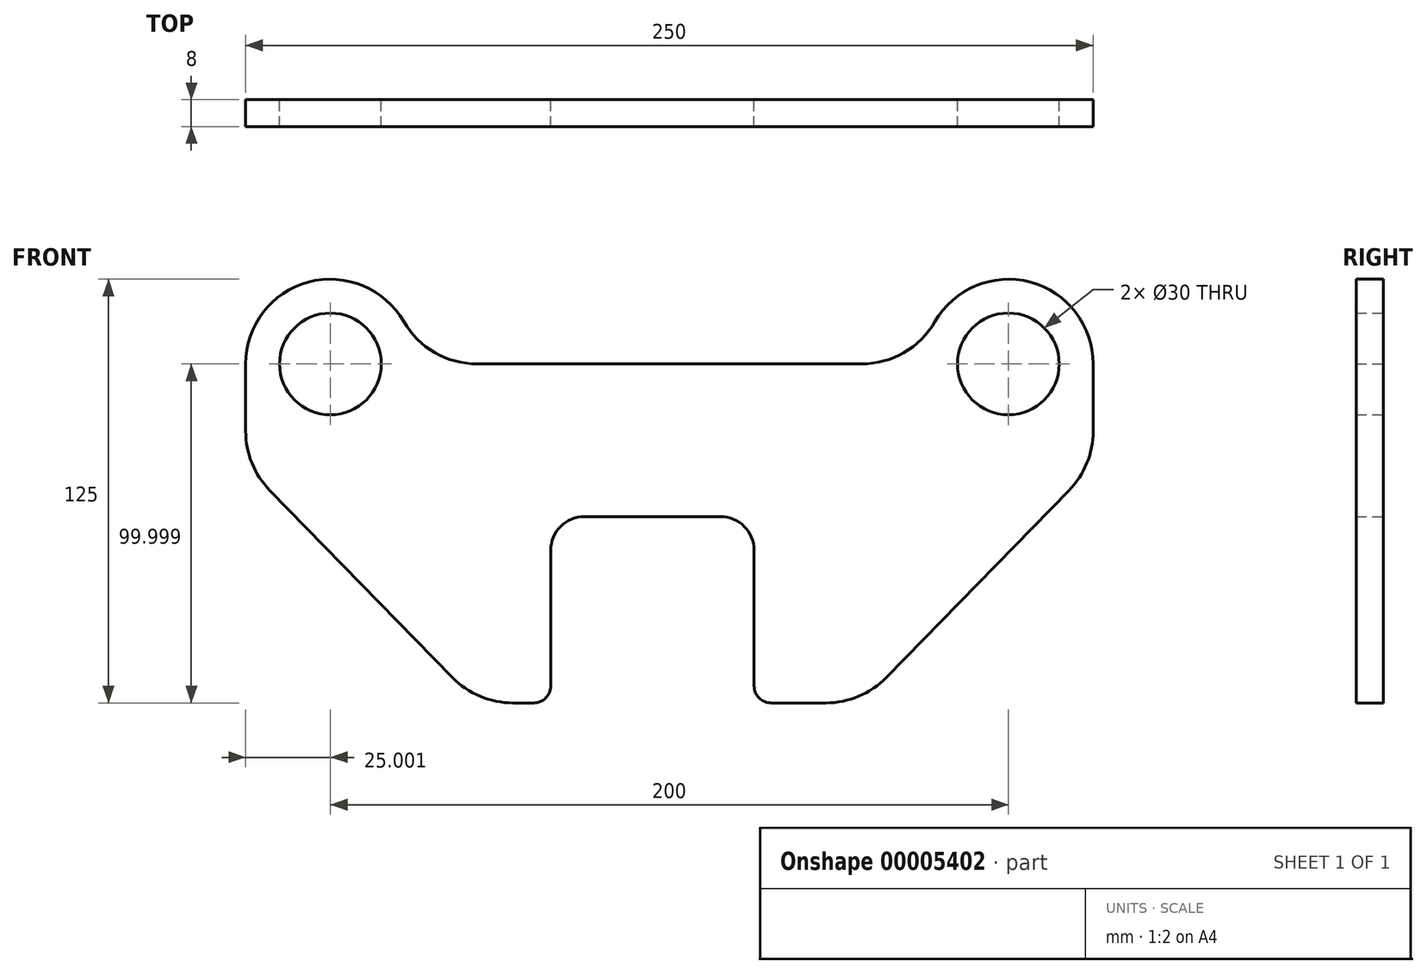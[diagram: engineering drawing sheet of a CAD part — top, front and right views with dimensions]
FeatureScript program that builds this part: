
annotation { "Feature Type Name" : "Feature", "Feature Type Description" : "" }
export const myFeature = defineFeature(function(context is Context, id is Id, definition is map)
    precondition{}
    {
        {
            var Q0;
            Q0=qCreatedBy(makeId("Front.planeOp"),FACE);
            var sketch = newSketch(context, id + "F0", { "sketchPlane" : qUnion([Q0])});
            skCircle(sketch, "E0", {"center": v(-79.29, 45.05) * mm, "radius": 15 * mm});
            skLineSegment(sketch, "E1", {"start": v(-35.99, 45.05) * mm, "end": v(77.41, 45.05) * mm});
            skCircle(sketch, "E2", {"center": v(120.71, 45.05) * mm, "radius": 15 * mm});
            skArc(sketch, "E3", {"start": v(-57.64, 57.55) * mm, "mid": v(-85.76, 69.2) * mm, "end": v(-104.29, 45.05) * mm});
            skArc(sketch, "E4", {"start": v(145.71, 45.05) * mm, "mid": v(127.18, 69.2) * mm, "end": v(99.06, 57.55) * mm});
            skArc(sketch, "E5.filletArc", {"start": v(-57.64, 57.55) * mm, "mid": v(-48.49, 48.4) * mm, "end": v(-35.99, 45.05) * mm});
            skArc(sketch, "E6.filletArc", {"start": v(77.41, 45.05) * mm, "mid": v(89.91, 48.4) * mm, "end": v(99.06, 57.55) * mm});
            skLineSegment(sketch, "E7.0", {"start": v(-25.45, -54.95) * mm, "end": v(-19.29, -54.95) * mm});
            skLineSegment(sketch, "E8", {"start": v(-104.29, 45.05) * mm, "end": v(-104.29, 25.23) * mm});
            skLineSegment(sketch, "E9", {"start": v(145.71, 45.05) * mm, "end": v(145.71, 25.23) * mm});
            skLineSegment(sketch, "E10", {"start": v(-97.18, 7.77) * mm, "end": v(-43.35, -47.41) * mm});
            skLineSegment(sketch, "E11", {"start": v(84.77, -47.41) * mm, "end": v(138.6, 7.77) * mm});
            skPoint(sketch, "E12.visualSharp", {"position": v(-104.29, 15.05) * mm});
            skArc(sketch, "E12.filletArc", {"start": v(-104.29, 25.23) * mm, "mid": v(-102.44, 15.8) * mm, "end": v(-97.18, 7.77) * mm});
            skPoint(sketch, "E13.visualSharp", {"position": v(145.71, 15.05) * mm});
            skArc(sketch, "E13.filletArc", {"start": v(138.6, 7.77) * mm, "mid": v(143.87, 15.8) * mm, "end": v(145.71, 25.23) * mm});
            skPoint(sketch, "E14.visualSharp", {"position": v(-35.99, -54.95) * mm});
            skArc(sketch, "E14.filletArc", {"start": v(-43.35, -47.41) * mm, "mid": v(-35.16, -52.99) * mm, "end": v(-25.45, -54.95) * mm});
            skPoint(sketch, "E15.visualSharp", {"position": v(77.41, -54.95) * mm});
            skArc(sketch, "E15.filletArc", {"start": v(66.87, -54.95) * mm, "mid": v(76.58, -52.99) * mm, "end": v(84.77, -47.41) * mm});
            skLineSegment(sketch, "E16.0", {"start": v(45.71, -49.95) * mm, "end": v(45.71, -9.95) * mm});
            skLineSegment(sketch, "E17.0", {"start": v(-14.29, -49.95) * mm, "end": v(-14.29, -9.95) * mm});
            skLineSegment(sketch, "E18", {"start": v(-4.29, 0.05) * mm, "end": v(35.71, 0.05) * mm});
            skLineSegment(sketch, "E19.trimOffspring", {"start": v(50.71, -54.95) * mm, "end": v(66.87, -54.95) * mm});
            skPoint(sketch, "E20.visualSharp", {"position": v(-14.29, 0.05) * mm});
            skArc(sketch, "E20.filletArc", {"start": v(-4.29, 0.05) * mm, "mid": v(-11.36, -2.88) * mm, "end": v(-14.29, -9.95) * mm});
            skPoint(sketch, "E21.visualSharp", {"position": v(45.71, 0.05) * mm});
            skArc(sketch, "E21.filletArc", {"start": v(45.71, -9.95) * mm, "mid": v(42.78, -2.88) * mm, "end": v(35.71, 0.05) * mm});
            skPoint(sketch, "E22.visualSharp", {"position": v(-14.29, -54.95) * mm});
            skArc(sketch, "E22.filletArc", {"start": v(-19.29, -54.95) * mm, "mid": v(-15.75, -53.49) * mm, "end": v(-14.29, -49.95) * mm});
            skPoint(sketch, "E23.visualSharp", {"position": v(45.71, -54.95) * mm});
            skArc(sketch, "E23.filletArc", {"start": v(45.71, -49.95) * mm, "mid": v(47.18, -53.49) * mm, "end": v(50.71, -54.95) * mm});
            skSolve(sketch);
        }
        {
            var Q0;
            Q0=makeQuery(id+"F0.imprint","IMPRINT",FACE,{"disambiguationData":[TD([[makeQuery(id+"F0.imprint","IMPRINT",EDGE,{"derivedFrom":sQuery(id+"F0.wireOp",EDGE,"E0")}),-1.0]])]});
            extrude(context, id + "F1", {"entities" : qUnion([Q0]), "depth" : 8 * mm});
        }
    });
